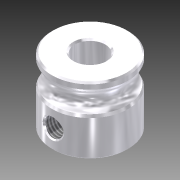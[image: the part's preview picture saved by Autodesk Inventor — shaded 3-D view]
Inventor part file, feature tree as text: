
AUTODESK INVENTOR PART (.ipt)
format: ipt  version: 2016 SP1 (Build 200210100, 210)  size: 177,664 bytes
history: native  units: in
note: dims shown in document units (in); Inventor stores cm internally (conversion verified against a paired STEP export)
features: sketch x4, extrude x3, revolve x1, chamfer x1, thread x1
ambient origin geometry x8: Origin, YZ Plane, XZ Plane, XY Plane, X Axis, Y Axis, Z Axis, Center Point
bodies: Solid1 (feature_tree)
feature tree (10):
  extrude  "Extrusion1"  Depth=0.433in TaperAngle=0.0deg
  revolve  "Revolution1"  [1 undecoded]
  extrude  "Extrusion2"  Depth=0.039in
  extrude  "Extrusion3"  Depth=0.433in
  chamfer  "Chamfer1"  Distance=0.433in
  thread  "Thread1"  [1 undecoded]
  sketch  "Sketch1"  dims[d0=0.496in d1=0.433in d2=0.0in]
  sketch  "Sketch2"  dims[d3=0.05in d4=0.14in]
  sketch  "Sketch3"  dims[d5=0.039in d6=0.039in]
  sketch  "Sketch4"  dims[d7=90.0deg d8=0.1969in d9=0.433in d10=0.0in d11=0.1181in d12=0.433in d13=0.0in d14=0.01in d15=0.125in d16=45.0deg d17=1.0in d18=0.0in]
note: 2 required parameter values undecoded (feature->parameter linkage not recoverable at this tier; creation-order binding heuristic only, values carry confidence <= 0.55)